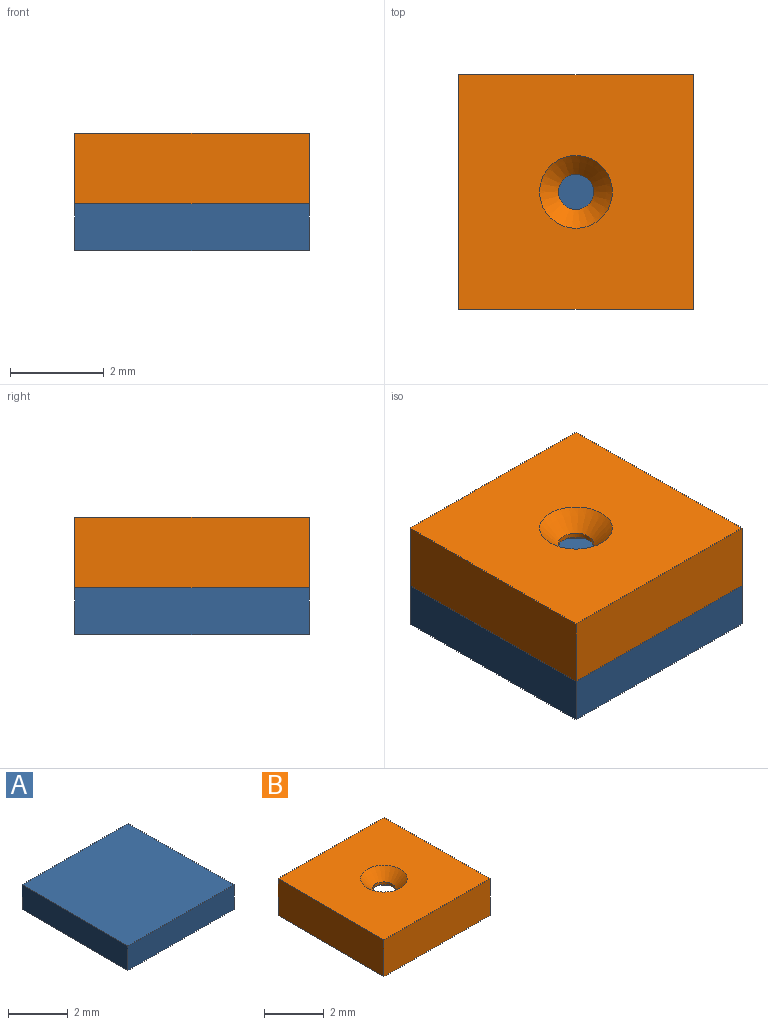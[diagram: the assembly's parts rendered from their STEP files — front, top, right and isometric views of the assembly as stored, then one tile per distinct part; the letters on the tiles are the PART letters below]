
ASSEMBLY  parts=2 mates=1
PART A: 6 faces, bbox 5x5x1 mm
  f0: plane 5x1mm, normal (0,-1,0), area 5mm2, adj f1,f3,f4,f5
  f1: plane 5x1mm, normal (1,0,0), area 5mm2, adj f0,f2,f4,f5
  f2: plane 5x1mm, normal (0,1,0), area 5mm2, adj f1,f3,f4,f5
  f3: plane 5x1mm, normal (-1,0,0), area 5mm2, adj f0,f2,f4,f5
  f4: plane 5x5mm, normal (0,0,1), area 25mm2, adj f0,f1,f2,f3
  f5: plane 5x5mm, normal (0,0,-1), area 25mm2, adj f0,f1,f2,f3
PART B: 10 faces, bbox 5x5x1.5 mm
  f0: plane 5x1.5mm, normal (0,-1,0), area 7.5mm2, adj f1,f3,f4,f5
  f1: plane 5x1.5mm, normal (1,0,0), area 7.5mm2, adj f0,f2,f4,f5
  f2: plane 5x1.5mm, normal (0,1,0), area 7.5mm2, adj f1,f3,f4,f5
  f3: plane 5x1.5mm, normal (-1,0,0), area 7.5mm2, adj f0,f2,f4,f5
  f4: plane 5x5mm, normal (0,0,1), area 23.1mm2, adj f0,f1,f2,f3,f9
  f5: plane 5x5mm, normal (0,0,-1), area 15.4mm2, adj f0,f1,f2,f3,f6
  f6: cylinder r=1.75mm len=3.5mm, axis (0,0,-1), area 11mm2, adj f5,f7
  f7: plane 3.5x3.5mm, normal (0,0,-1), area 9.2mm2, adj f6,f8
  f8: cylinder r=0.38mm len=0.75mm, axis (0,0,1), area 0.2mm2, adj f7,f9
  f9: cone r=0.38mm half-angle=45deg, axis (0,0,1), area 2mm2, adj f4,f8
PLACE A t=(-0.06,0.22,-1.11)mm
PLACE B t=(-0.06,0.22,-0.11)mm
MATE planar A.f4 <-> B.f6  axis (0,0,1) through (-0.06,0.22,-0.11)mm
